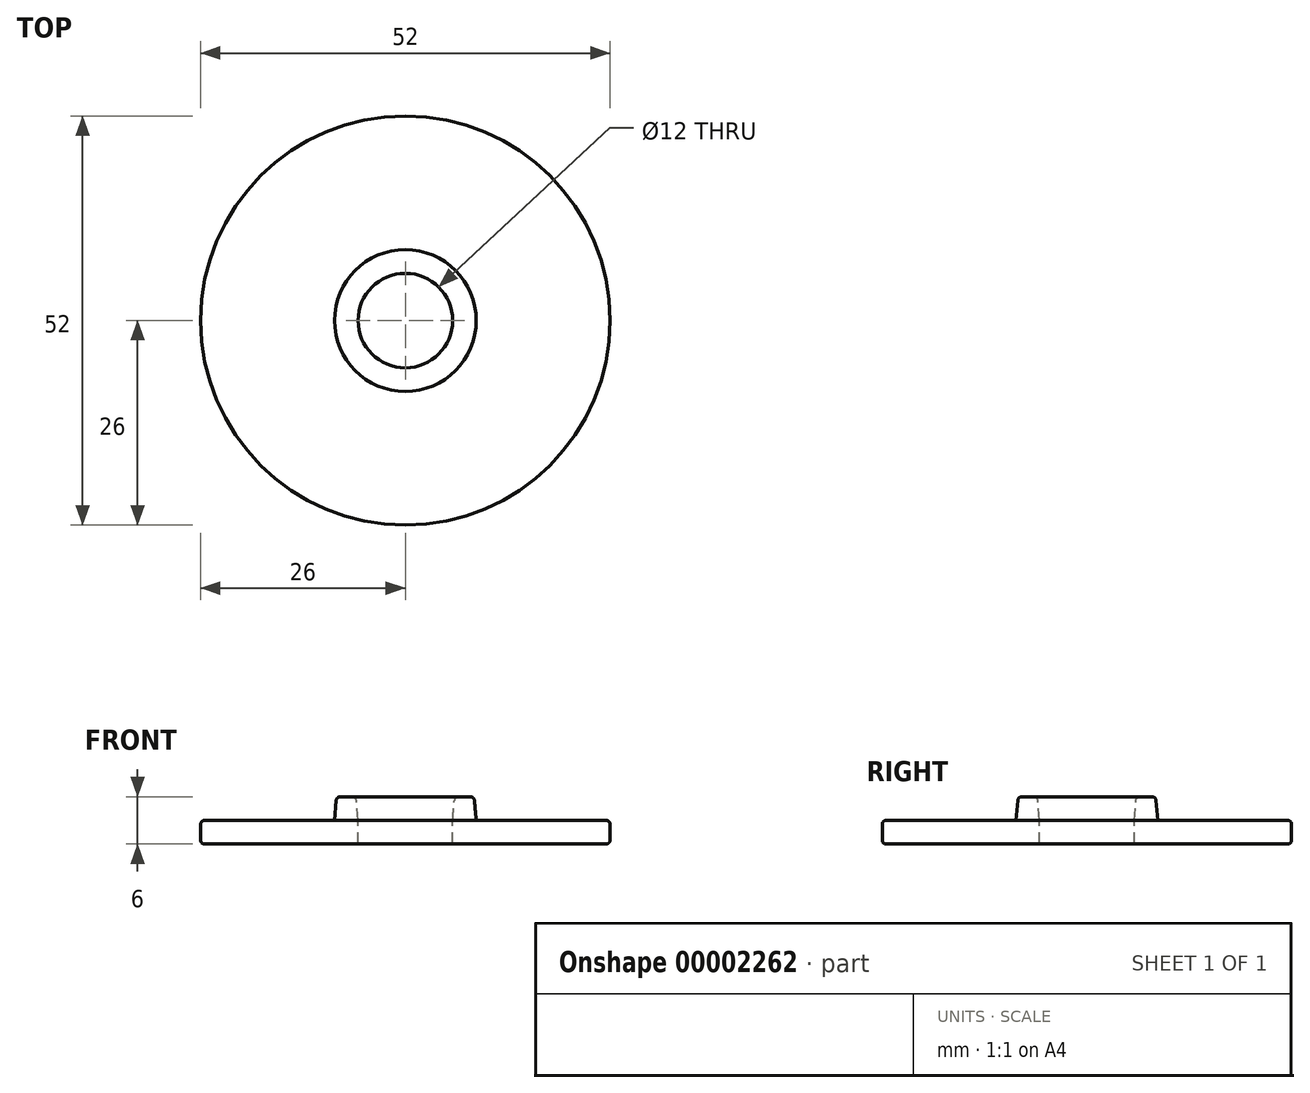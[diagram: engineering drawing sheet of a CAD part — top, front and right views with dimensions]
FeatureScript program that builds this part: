
annotation { "Feature Type Name" : "Feature", "Feature Type Description" : "" }
export const myFeature = defineFeature(function(context is Context, id is Id, definition is map)
    precondition{}
    {
        {
            var Q0;
            Q0=qCreatedBy(makeId("Top.planeOp"),FACE);
            var sketch = newSketch(context, id + "F0", { "sketchPlane" : qUnion([Q0])});
            skCircle(sketch, "E0", {"center": v(0, 0) * mm, "radius": 26 * mm});
            skCircle(sketch, "E1", {"center": v(0, 0) * mm, "radius": 9 * mm});
            skCircle(sketch, "E2", {"center": v(0, 0) * mm, "radius": 6 * mm});
            skSolve(sketch);
        }
        {
            var Q0;
            Q0=makeQuery(id+"F0.imprint","IMPRINT",FACE,{"disambiguationData":[TD([[makeQuery(id+"F0.imprint","IMPRINT",EDGE,{"derivedFrom":sQuery(id+"F0.wireOp",EDGE,"E1")}),1.0]])]});
            var Q1;
            Q1=makeQuery(id+"F0.imprint","IMPRINT",FACE,{"disambiguationData":[TD([[makeQuery(id+"F0.imprint","IMPRINT",EDGE,{"derivedFrom":sQuery(id+"F0.wireOp",EDGE,"E0")}),1.0]])]});
            extrude(context, id + "F1", {"entities" : qUnion([Q0, Q1]), "oppositeDirection" : true, "depth" : 3 * mm});
        }
        {
            var Q0;
            Q0=makeQuery(id+"F0.imprint","IMPRINT",FACE,{"disambiguationData":[TD([[makeQuery(id+"F0.imprint","IMPRINT",EDGE,{"derivedFrom":sQuery(id+"F0.wireOp",EDGE,"E1")}),1.0]])]});
            extrude(context, id + "F2", {"entities" : qUnion([Q0]), "operationType" : NewBodyOperationType.ADD, "depth" : 3 * mm, "hasDraft" : true, "draftAngle" : 5 * degree, "draftPullDirection" : true});
        }
        {
            var Q0;
            Q0=makeQuery(id+"F1.opExtrude","CAP_EDGE",EDGE,{"disambiguationData":[OSD([sQuery(id+"F0.wireOp",EDGE,"E0")])],"isStart":true});
            var Q1;
            Q1=makeQuery(id+"F1.opExtrude","CAP_EDGE",EDGE,{"disambiguationData":[OSD([sQuery(id+"F0.wireOp",EDGE,"E0")])],"isStart":false});
            var Q2;
            Q2=makeQuery(id+"F2.opExtrude","CAP_EDGE",EDGE,{"disambiguationData":[OSD([sQuery(id+"F0.wireOp",EDGE,"E1")])],"isStart":false});
            var Q3;
            Q3=makeQuery(id+"F2.opExtrude","CAP_EDGE",EDGE,{"disambiguationData":[OSD([sQuery(id+"F0.wireOp",EDGE,"E2")])],"isStart":false});
            var Q4;
            Q4=makeQuery(id+"F2.opExtrude","CAP_EDGE",EDGE,{"disambiguationData":[OSD([sQuery(id+"F0.wireOp",EDGE,"E1")])],"isStart":true});
            fillet(context, id + "F3", {"entities" : qUnion([Q0, Q1, Q2, Q3, Q4]), "radius" : .5 * mm, "tangentPropagation" : true, "allowEdgeOverflow" : false});
        }
    });
